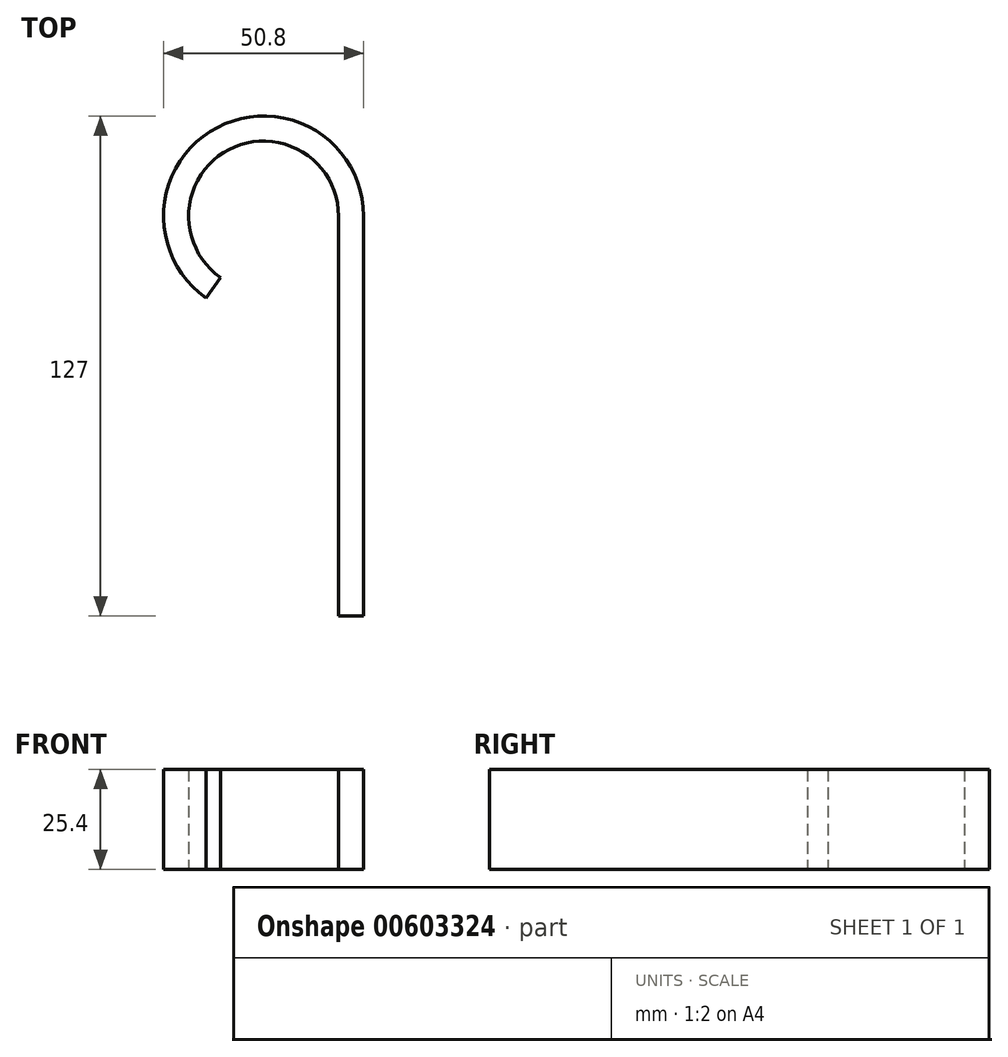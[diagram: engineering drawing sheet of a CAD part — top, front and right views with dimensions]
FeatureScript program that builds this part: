
annotation { "Feature Type Name" : "Feature", "Feature Type Description" : "" }
export const myFeature = defineFeature(function(context is Context, id is Id, definition is map)
    precondition{}
    {
        {
            var Q0;
            Q0=qCreatedBy(makeId("Top.planeOp"),FACE);
            var sketch = newSketch(context, id + "F0", { "sketchPlane" : qUnion([Q0])});
            skArc(sketch, "E0", {"start": v(19.05, 0) * mm, "mid": v(-8.8, 16.9) * mm, "end": v(-10.93, -15.6) * mm});
            skArc(sketch, "E1", {"start": v(25.4, 0) * mm, "mid": v(-11.73, 22.53) * mm, "end": v(-14.57, -20.8) * mm});
            skLineSegment(sketch, "E2", {"start": v(19.05, 0) * mm, "end": v(19.05, -101.6) * mm});
            skLineSegment(sketch, "E3", {"start": v(25.4, 0) * mm, "end": v(25.4, -101.6) * mm});
            skLineSegment(sketch, "E4", {"start": v(25.4, -101.6) * mm, "end": v(19.05, -101.6) * mm});
            skLineSegment(sketch, "E5", {"start": v(-14.57, -20.8) * mm, "end": v(-10.93, -15.6) * mm});
            skSolve(sketch);
        }
        {
            var Q0;
            Q0=makeQuery(id+"F0.imprint","IMPRINT",FACE,{"disambiguationData":[TD([[makeQuery(id+"F0.imprint","IMPRINT",EDGE,{"derivedFrom":sQuery(id+"F0.wireOp",EDGE,"E0")}),-1.0]])]});
            extrude(context, id + "F1", {"entities" : qUnion([Q0]), "depth" : 25.4 * mm, "offsetDistance" : 25.4 * mm});
        }
    });
